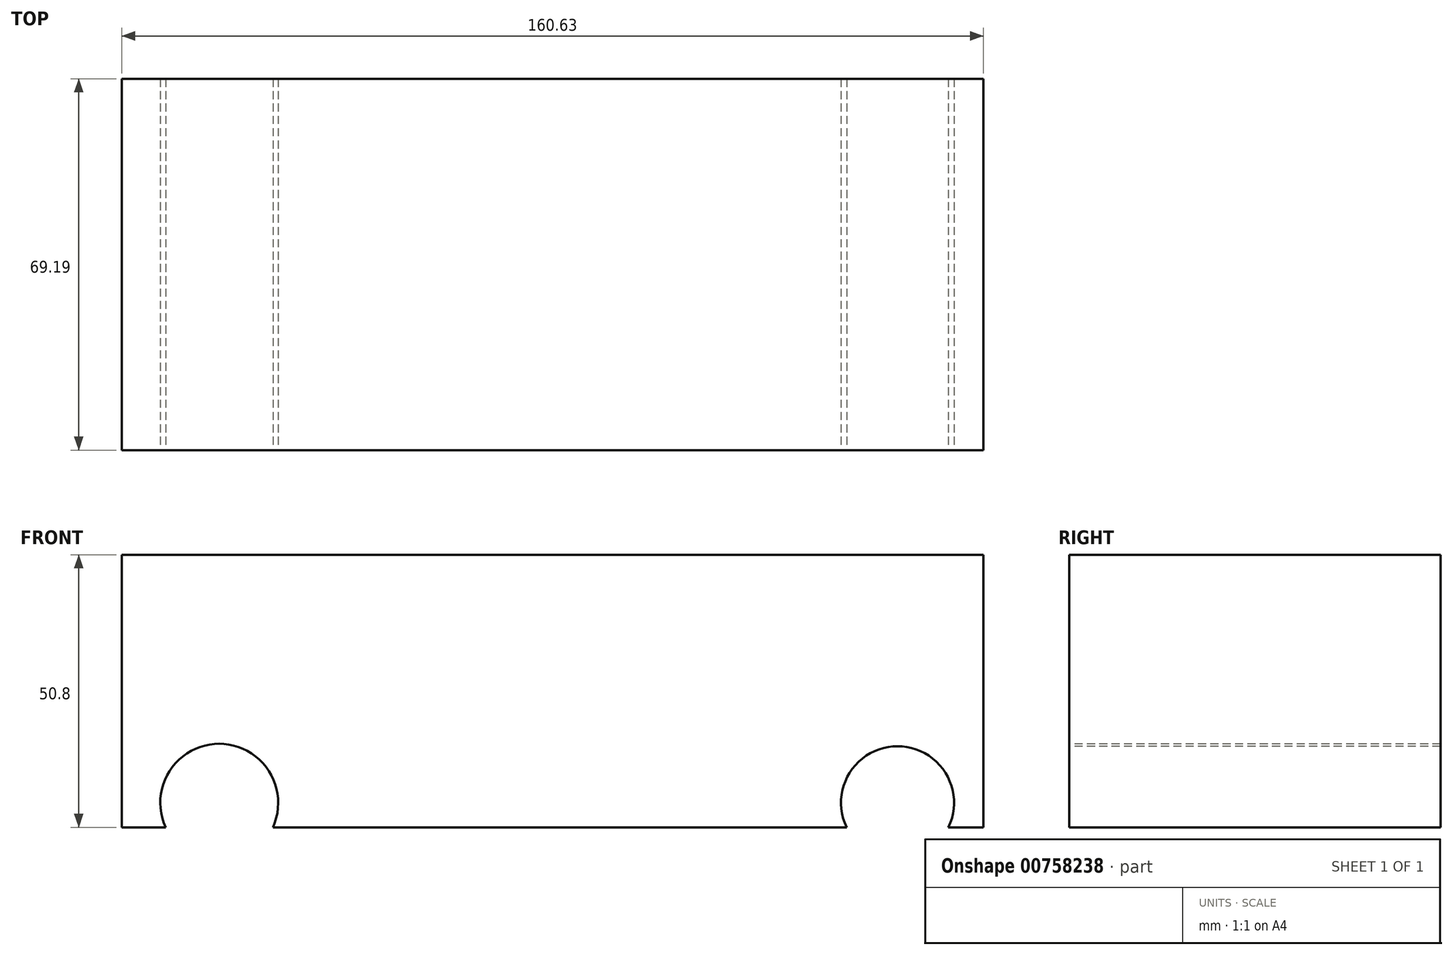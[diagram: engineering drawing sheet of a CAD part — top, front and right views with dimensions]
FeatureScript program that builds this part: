
annotation { "Feature Type Name" : "Feature", "Feature Type Description" : "" }
export const myFeature = defineFeature(function(context is Context, id is Id, definition is map)
    precondition{}
    {
        {
            var Q0;
            Q0=qCreatedBy(makeId("Top.planeOp"),FACE);
            var sketch = newSketch(context, id + "F0", { "sketchPlane" : qUnion([Q0])});
            skLineSegment(sketch, "E0.bottom", {"start": v(-80.62, 28.65) * mm, "end": v(80, 28.65) * mm});
            skLineSegment(sketch, "E0.top", {"start": v(-80.62, -40.54) * mm, "end": v(80, -40.54) * mm});
            skLineSegment(sketch, "E0.left", {"start": v(-80.62, 28.65) * mm, "end": v(-80.62, -40.54) * mm});
            skLineSegment(sketch, "E0.right", {"start": v(80, 28.65) * mm, "end": v(80, -40.54) * mm});
            skSolve(sketch);
        }
        {
            var Q0;
            Q0 = qSketchRegion(id + "F0", true);
            extrude(context, id + "F1", {"entities" : qUnion([Q0]), "depth" : 50.8 * mm, "offsetDistance" : 25.4 * mm});
        }
        {
            var Q0;
            Q0=makeQuery(id+"F1.opExtrude","SWEPT_FACE",FACE,{"disambiguationData":[OSD([sQuery(id+"F0.wireOp",EDGE,"E0.top")])]});
            var sketch = newSketch(context, id + "F2", { "sketchPlane" : qUnion([Q0])});
            skCircle(sketch, "E1", {"center": v(-62.43, 4.57) * mm, "radius": 11 * mm});
            skCircle(sketch, "E2", {"center": v(64, 4.57) * mm, "radius": 10.54 * mm});
            skSolve(sketch);
        }
        {
            var Q0;
            Q0 = qSketchRegion(id + "F2", true);
            extrude(context, id + "F3", {"entities" : qUnion([Q0]), "operationType" : NewBodyOperationType.REMOVE, "oppositeDirection" : true, "depth" : 127 * mm, "offsetDistance" : 25.4 * mm});
        }
    });
